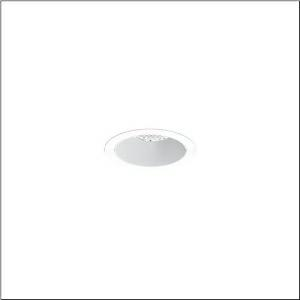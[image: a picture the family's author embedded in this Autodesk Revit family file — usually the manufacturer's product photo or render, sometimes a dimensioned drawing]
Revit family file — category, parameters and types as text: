
# Revit family: lunis_21_m_51db18ec91c
name_source: partatom
category: Lighting Fixtures
units: mm (PartAtom-declared; Revit-internal decimal feet)

## family parameters
Cut with Voids When Loaded = No
Host = Face
Light Source = No
Part Type = Normal
Room Calculation Point = No
Round Connector Dimension = Use Diameter
Shared = No

## types (1)
- --- (1 x LED, 3870 lm, 25.5 W, 6500K)
    Apparent Load = 26 VA
    CIE Flux Codes = 86 95 99 100 100
    Color Rendering = 80
    Color Temperature = 6500K
    Default Elevation = 1800 mm
    Description = Lunis 21,  M, downlight, light control with lens, of PMMA, anti glare with reflector, of PC, light emission: direct distribution, LED rated luminous flux: 1.800lm, light colour: 830/840/865, with terminal, 5-pole, mains connection: 220..240V, AC/DC, 0/50..60Hz, housing, round, of diecast aluminium, traffic white (RAL 9016), diameter: 115mm, clamping range: 1..40mm, protection rating (complete): IP20, protection rating (on room side): IP54, insulation class (complete): insulation class II (safety insulation), certification: CE, impact resistance: IK03, packaging unit: 1 piece
    Height = 0 mm  [stored 0 ft]
    Lamp = 1 x LED
    Lamp Light Flux = 3870 lm
    Lamp Power = 25.5 W
    Lamp count = 1
    Length = 115 mm
    Luminous efficacy = 152 lm/W
    Manufacturer = Siteco
    ModVariant = No
    Model = 51DB18EC91C
    Mounting Place = Ceiling
    Mounting Type = Recessed
    Number of Poles = 1
    OnlyDefault = Yes
    Power Factor = 1
    Product Name = Lunis 21 M
    Product group = downlight
    ProductGroupID = 400
    Protection Class = Protection class II
    Protection Degree = IP 20
    RLX_Detail_Level = 1
    RLX_Emergency_Light_Flux = 0 lm
    RLX_Emergency_Type = 0
    RLX_Emergency_Type_DB = No
    RlxData = <blob elided: 14065 chars, md5=fbd0e5eb>
    Socket = socket
    Standby Power = 0 W
    System Light Flux = 3870 lm
    System Power = 26 W
    Type Comments = individual setting: colour temperature 6500K, luminous flux: 100 % | (ON | ON | OFF | OFF) | 700 mA
    Type Image = l_1290852.jpg
    URL = http://relux.com
    VarID = @adj_019538
    Voltage = 0 V
    Weight = 0.00 kg
    Width = 0 mm  [stored 0 ft]

note: [stored X ft] marks values corroborated as IEEE doubles in the binary element streams (Revit-internal decimal feet)

## geometry (parser evidence)
native form markers: Sweep x10
no freeform markers — native parametric forms only
